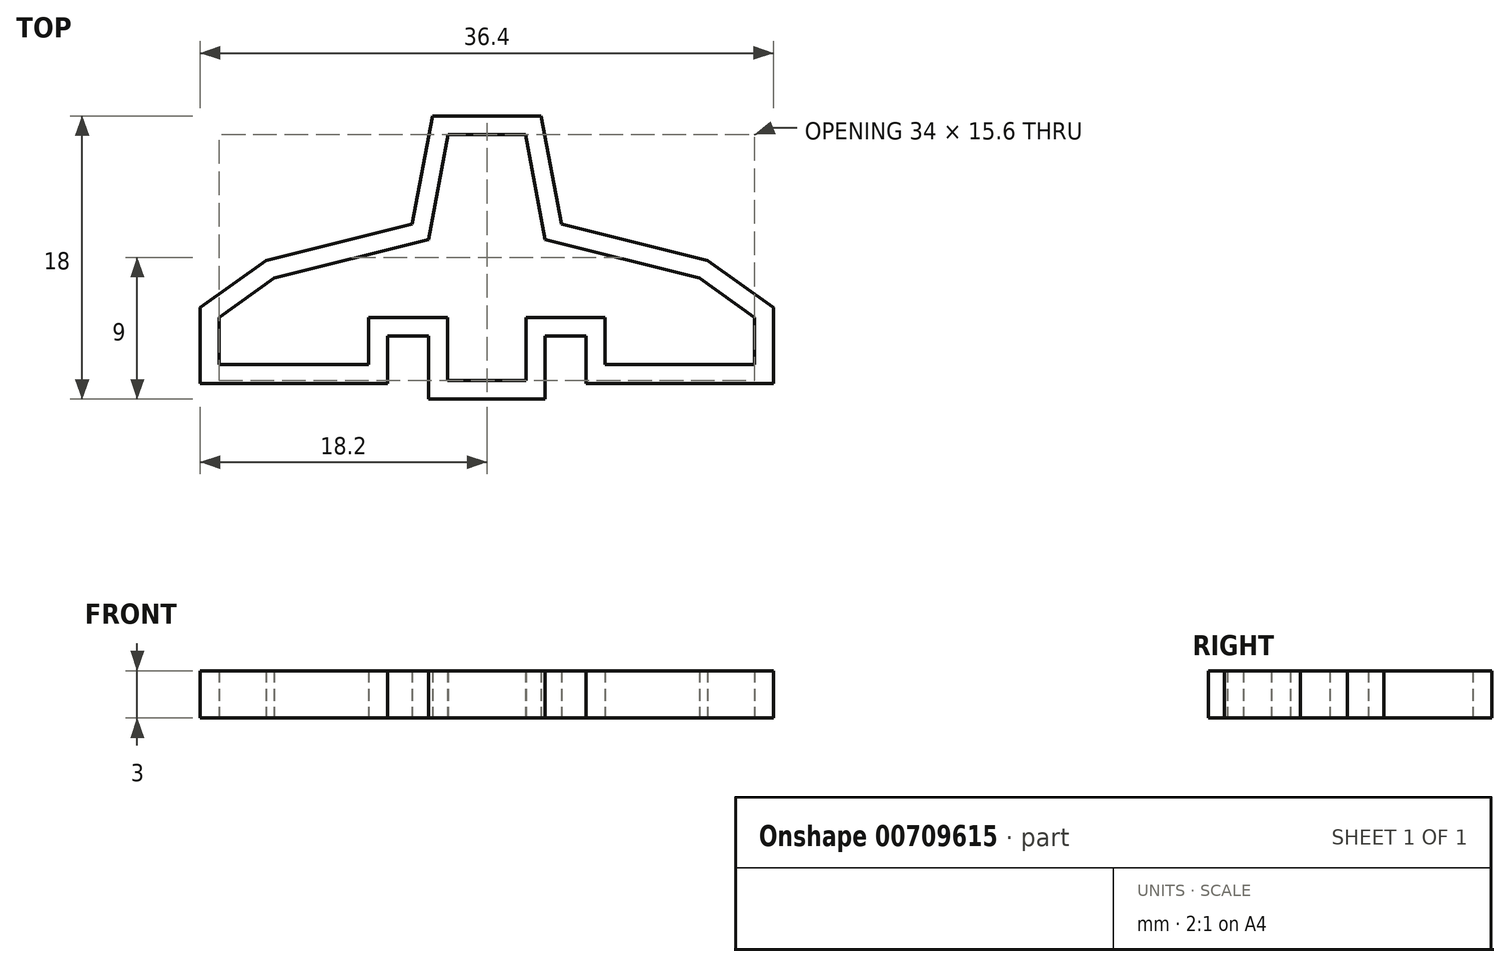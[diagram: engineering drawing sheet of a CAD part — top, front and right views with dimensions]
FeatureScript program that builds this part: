
annotation { "Feature Type Name" : "Feature", "Feature Type Description" : "" }
export const myFeature = defineFeature(function(context is Context, id is Id, definition is map)
    precondition{}
    {
        {
            var Q0;
            Q0=qCreatedBy(makeId("Top.planeOp"),FACE);
            var sketch = newSketch(context, id + "F0", { "sketchPlane" : qUnion([Q0])});
            skLineSegment(sketch, "E0", {"start": v(2.5, -5.5) * mm, "end": v(2.5, -1.5) * mm});
            skLineSegment(sketch, "E1", {"start": v(2.5, -1.5) * mm, "end": v(7.5, -1.5) * mm});
            skLineSegment(sketch, "E2", {"start": v(7.5, -1.5) * mm, "end": v(7.5, -4.5) * mm});
            skPoint(sketch, "E3.visualSharp", {"position": v(7.5, -1.5) * mm});
            skPoint(sketch, "E4.visualSharp", {"position": v(2.5, -1.5) * mm});
            skPoint(sketch, "E5.visualSharp", {"position": v(7.5, -4.5) * mm});
            skLineSegment(sketch, "E6.top", {"start": v(68.94, -3) * mm, "end": v(61.94, -3) * mm});
            skLineSegment(sketch, "E6.left", {"start": v(69.94, -0.2) * mm, "end": v(69.94, -2) * mm});
            skPoint(sketch, "E6.middle", {"position": v(53.44, 1.5) * mm});
            skLineSegment(sketch, "E7", {"start": v(53.44, 14) * mm, "end": v(54.6, 14) * mm});
            skLineSegment(sketch, "E8", {"start": v(55.59, 13.18) * mm, "end": v(56.82, 6.6) * mm});
            skLineSegment(sketch, "E9", {"start": v(57.52, 5.82) * mm, "end": v(66.81, 3.04) * mm});
            skLineSegment(sketch, "E10", {"start": v(69.79, 0.15) * mm, "end": v(67.02, 2.9) * mm});
            skLineSegment(sketch, "E11", {"start": v(55.94, -4) * mm, "end": v(55.94, -0.5) * mm});
            skLineSegment(sketch, "E12", {"start": v(56.44, 0) * mm, "end": v(60.44, 0) * mm});
            skLineSegment(sketch, "E13", {"start": v(60.94, -0.5) * mm, "end": v(60.94, -2) * mm});
            skPoint(sketch, "E14.visualSharp", {"position": v(60.94, 0) * mm});
            skArc(sketch, "E14.filletArc", {"start": v(60.94, -0.5) * mm, "mid": v(60.79, -0.15) * mm, "end": v(60.44, 0) * mm});
            skPoint(sketch, "E15.visualSharp", {"position": v(55.94, 0) * mm});
            skArc(sketch, "E15.filletArc", {"start": v(56.44, 0) * mm, "mid": v(56.08, -0.15) * mm, "end": v(55.94, -0.5) * mm});
            skPoint(sketch, "E16.visualSharp", {"position": v(60.94, -3) * mm});
            skArc(sketch, "E16.filletArc", {"start": v(60.94, -2) * mm, "mid": v(61.23, -2.7) * mm, "end": v(61.94, -3) * mm});
            skPoint(sketch, "E17.visualSharp", {"position": v(66.94, 3) * mm});
            skArc(sketch, "E17.filletArc", {"start": v(67.02, 2.9) * mm, "mid": v(66.93, 2.99) * mm, "end": v(66.81, 3.04) * mm});
            skPoint(sketch, "E18.visualSharp", {"position": v(69.94, 0) * mm});
            skArc(sketch, "E18.filletArc", {"start": v(69.94, -0.2) * mm, "mid": v(69.9, -0.02) * mm, "end": v(69.79, 0.15) * mm});
            skPoint(sketch, "E19.visualSharp", {"position": v(69.94, -3) * mm});
            skArc(sketch, "E19.filletArc", {"start": v(68.94, -3) * mm, "mid": v(69.64, -2.7) * mm, "end": v(69.94, -2) * mm});
            skPoint(sketch, "E20.visualSharp", {"position": v(56.94, 6) * mm});
            skArc(sketch, "E20.filletArc", {"start": v(56.82, 6.6) * mm, "mid": v(57.06, 6.11) * mm, "end": v(57.52, 5.82) * mm});
            skPoint(sketch, "E21.visualSharp", {"position": v(55.44, 14) * mm});
            skArc(sketch, "E21.filletArc", {"start": v(55.59, 13.18) * mm, "mid": v(55.24, 13.77) * mm, "end": v(54.6, 14) * mm});
            skLineSegment(sketch, "E22", {"start": v(53.44, 18.4) * mm, "end": v(53.44, -13.46) * mm, "construction": true});
            skLineSegment(sketch, "E23", {"start": v(55.94, -4) * mm, "end": v(53.44, -4) * mm});
            skLineSegment(sketch, "E24.top", {"start": v(62.7, -29.7) * mm, "end": v(54.7, -29.7) * mm});
            skLineSegment(sketch, "E24.left", {"start": v(62.7, -26.7) * mm, "end": v(62.7, -29.7) * mm});
            skPoint(sketch, "E24.middle", {"position": v(46.2, -25.2) * mm});
            skLineSegment(sketch, "E25", {"start": v(46.2, -12.7) * mm, "end": v(48.2, -12.7) * mm});
            skLineSegment(sketch, "E26", {"start": v(48.2, -12.7) * mm, "end": v(49.48, -19.5) * mm});
            skLineSegment(sketch, "E27", {"start": v(50.87, -21.05) * mm, "end": v(59.7, -23.7) * mm});
            skLineSegment(sketch, "E28", {"start": v(62.7, -26.7) * mm, "end": v(59.7, -23.7) * mm});
            skLineSegment(sketch, "E29", {"start": v(48.7, -30.7) * mm, "end": v(48.7, -27.2) * mm});
            skLineSegment(sketch, "E30", {"start": v(49.2, -26.7) * mm, "end": v(53.2, -26.7) * mm});
            skLineSegment(sketch, "E31", {"start": v(53.7, -27.2) * mm, "end": v(53.7, -28.7) * mm});
            skPoint(sketch, "E32.visualSharp", {"position": v(53.7, -26.7) * mm});
            skArc(sketch, "E32.filletArc", {"start": v(53.7, -27.2) * mm, "mid": v(53.55, -26.85) * mm, "end": v(53.2, -26.7) * mm});
            skPoint(sketch, "E33.visualSharp", {"position": v(48.7, -26.7) * mm});
            skArc(sketch, "E33.filletArc", {"start": v(49.2, -26.7) * mm, "mid": v(48.85, -26.85) * mm, "end": v(48.7, -27.2) * mm});
            skPoint(sketch, "E34.visualSharp", {"position": v(53.7, -29.7) * mm});
            skArc(sketch, "E34.filletArc", {"start": v(53.7, -28.7) * mm, "mid": v(54, -29.4) * mm, "end": v(54.7, -29.7) * mm});
            skPoint(sketch, "E35.visualSharp", {"position": v(59.7, -23.7) * mm});
            skLineSegment(sketch, "E35.filletArc", {"start": v(59.7, -23.7) * mm, "end": v(59.7, -23.7) * mm});
            skPoint(sketch, "E36.visualSharp", {"position": v(62.7, -26.7) * mm});
            skLineSegment(sketch, "E36.filletArc", {"start": v(62.7, -26.7) * mm, "end": v(62.7, -26.7) * mm});
            skPoint(sketch, "E37.visualSharp", {"position": v(62.7, -29.7) * mm});
            skLineSegment(sketch, "E37.filletArc", {"start": v(62.7, -29.7) * mm, "end": v(62.7, -29.7) * mm});
            skPoint(sketch, "E38.visualSharp", {"position": v(49.7, -20.7) * mm});
            skArc(sketch, "E38.filletArc", {"start": v(49.48, -19.5) * mm, "mid": v(49.95, -20.47) * mm, "end": v(50.87, -21.05) * mm});
            skPoint(sketch, "E39.visualSharp", {"position": v(48.2, -12.7) * mm});
            skLineSegment(sketch, "E39.filletArc", {"start": v(48.2, -12.7) * mm, "end": v(48.2, -12.7) * mm});
            skLineSegment(sketch, "E40", {"start": v(46.2, -8.3) * mm, "end": v(46.2, -40.16) * mm, "construction": true});
            skLineSegment(sketch, "E41", {"start": v(48.7, -30.7) * mm, "end": v(46.2, -30.7) * mm});
            skLineSegment(sketch, "E42", {"start": v(2.5, -5.5) * mm, "end": v(0, -5.5) * mm});
            skLineSegment(sketch, "E43", {"start": v(2.45, 10.1) * mm, "end": v(0, 10.1) * mm});
            skLineSegment(sketch, "E44", {"start": v(17, -4.5) * mm, "end": v(17, -1.5) * mm});
            skLineSegment(sketch, "E45", {"start": v(3.7, 3.45) * mm, "end": v(13.5, 1) * mm});
            skLineSegment(sketch, "E46", {"start": v(13.5, 1) * mm, "end": v(17, -1.5) * mm});
            skLineSegment(sketch, "E47", {"start": v(7.5, -4.5) * mm, "end": v(17, -4.5) * mm});
            skLineSegment(sketch, "E48", {"start": v(2.45, 10.1) * mm, "end": v(3.7, 3.45) * mm});
            skLineSegment(sketch, "E49", {"start": v(43.9, -56.14) * mm, "end": v(43.9, -52.14) * mm});
            skLineSegment(sketch, "E50", {"start": v(43.9, -52.14) * mm, "end": v(48.9, -52.14) * mm});
            skLineSegment(sketch, "E51", {"start": v(48.9, -52.14) * mm, "end": v(48.9, -55.14) * mm});
            skPoint(sketch, "E52.visualSharp", {"position": v(48.9, -52.14) * mm});
            skPoint(sketch, "E53.visualSharp", {"position": v(43.9, -52.14) * mm});
            skPoint(sketch, "E54.visualSharp", {"position": v(48.9, -55.14) * mm});
            skLineSegment(sketch, "E55", {"start": v(43.9, -56.14) * mm, "end": v(41.4, -56.14) * mm});
            skLineSegment(sketch, "E56", {"start": v(43.86, -40.54) * mm, "end": v(41.4, -40.54) * mm});
            skLineSegment(sketch, "E57", {"start": v(58.4, -55.14) * mm, "end": v(58.4, -52.14) * mm});
            skLineSegment(sketch, "E58", {"start": v(45.1, -47.2) * mm, "end": v(54.9, -49.64) * mm});
            skLineSegment(sketch, "E59", {"start": v(54.9, -49.64) * mm, "end": v(58.4, -52.14) * mm});
            skLineSegment(sketch, "E60", {"start": v(48.9, -55.14) * mm, "end": v(58.4, -55.14) * mm});
            skLineSegment(sketch, "E61", {"start": v(43.86, -40.54) * mm, "end": v(45.1, -47.2) * mm});
            skLineSegment(sketch, "E62", {"start": v(0, 13.69) * mm, "end": v(0, -12.11) * mm, "construction": true});
            skLineSegment(sketch, "E63.MirrorCS", {"start": v(-2.45, 10.1) * mm, "end": v(0, 10.1) * mm});
            skLineSegment(sketch, "E64.MirrorCS", {"start": v(-7.5, -1.5) * mm, "end": v(-7.5, -4.5) * mm});
            skLineSegment(sketch, "E65.MirrorCS", {"start": v(-2.5, -1.5) * mm, "end": v(-7.5, -1.5) * mm});
            skLineSegment(sketch, "E66.MirrorCS", {"start": v(-2.5, -5.5) * mm, "end": v(0, -5.5) * mm});
            skLineSegment(sketch, "E67.MirrorCS", {"start": v(-7.5, -4.5) * mm, "end": v(-17, -4.5) * mm});
            skLineSegment(sketch, "E68.MirrorCS", {"start": v(-2.5, -5.5) * mm, "end": v(-2.5, -1.5) * mm});
            skPoint(sketch, "E69.MirrorP", {"position": v(-2.5, -1.5) * mm});
            skPoint(sketch, "E70.MirrorP", {"position": v(-7.5, -4.5) * mm});
            skPoint(sketch, "E71.MirrorP", {"position": v(-7.5, -1.5) * mm});
            skLineSegment(sketch, "E72.MirrorCS", {"start": v(-17, -4.5) * mm, "end": v(-17, -1.5) * mm});
            skLineSegment(sketch, "E73.MirrorCS", {"start": v(-3.7, 3.45) * mm, "end": v(-13.5, 1) * mm});
            skLineSegment(sketch, "E74.MirrorCS", {"start": v(-2.45, 10.1) * mm, "end": v(-3.7, 3.45) * mm});
            skLineSegment(sketch, "E75.MirrorCS", {"start": v(-13.5, 1) * mm, "end": v(-17, -1.5) * mm});
            skLineSegment(sketch, "E76.0", {"start": v(3.7, -6.7) * mm, "end": v(0, -6.7) * mm});
            skLineSegment(sketch, "E76.1", {"start": v(-3.7, -6.7) * mm, "end": v(0, -6.7) * mm});
            skLineSegment(sketch, "E76.2", {"start": v(-3.7, -6.7) * mm, "end": v(-3.7, -2.7) * mm});
            skLineSegment(sketch, "E76.3", {"start": v(-3.7, -2.7) * mm, "end": v(-6.3, -2.7) * mm});
            skLineSegment(sketch, "E76.4", {"start": v(-6.3, -2.7) * mm, "end": v(-6.3, -5.7) * mm});
            skLineSegment(sketch, "E76.5", {"start": v(3.7, -6.7) * mm, "end": v(3.7, -2.7) * mm});
            skLineSegment(sketch, "E76.6", {"start": v(-6.3, -5.7) * mm, "end": v(-18.2, -5.7) * mm});
            skLineSegment(sketch, "E76.7", {"start": v(-18.2, -5.7) * mm, "end": v(-18.2, -0.88) * mm});
            skLineSegment(sketch, "E76.8", {"start": v(-14.01, 2.1) * mm, "end": v(-18.2, -0.88) * mm});
            skLineSegment(sketch, "E76.9", {"start": v(-4.73, 4.43) * mm, "end": v(-14.01, 2.1) * mm});
            skLineSegment(sketch, "E76.10", {"start": v(18.2, -5.7) * mm, "end": v(18.2, -0.88) * mm});
            skLineSegment(sketch, "E76.11", {"start": v(6.3, -5.7) * mm, "end": v(18.2, -5.7) * mm});
            skLineSegment(sketch, "E76.12", {"start": v(6.3, -2.7) * mm, "end": v(6.3, -5.7) * mm});
            skLineSegment(sketch, "E76.13", {"start": v(3.7, -2.7) * mm, "end": v(6.3, -2.7) * mm});
            skLineSegment(sketch, "E76.14", {"start": v(14.01, 2.1) * mm, "end": v(18.2, -0.88) * mm});
            skLineSegment(sketch, "E76.15", {"start": v(4.73, 4.43) * mm, "end": v(14.01, 2.1) * mm});
            skLineSegment(sketch, "E76.16", {"start": v(3.45, 11.3) * mm, "end": v(4.73, 4.43) * mm});
            skLineSegment(sketch, "E76.17", {"start": v(3.45, 11.3) * mm, "end": v(0, 11.3) * mm});
            skLineSegment(sketch, "E76.18", {"start": v(-3.45, 11.3) * mm, "end": v(0, 11.3) * mm});
            skLineSegment(sketch, "E76.19", {"start": v(-3.45, 11.3) * mm, "end": v(-4.73, 4.43) * mm});
            skSolve(sketch);
        }
        {
            var Q0;
            Q0 = qSketchRegion(id + "F0", true);
            extrude(context, id + "F1", {"entities" : qUnion([Q0]), "depth" : 3 * mm, "offsetDistance" : 25 * mm});
        }
    });
